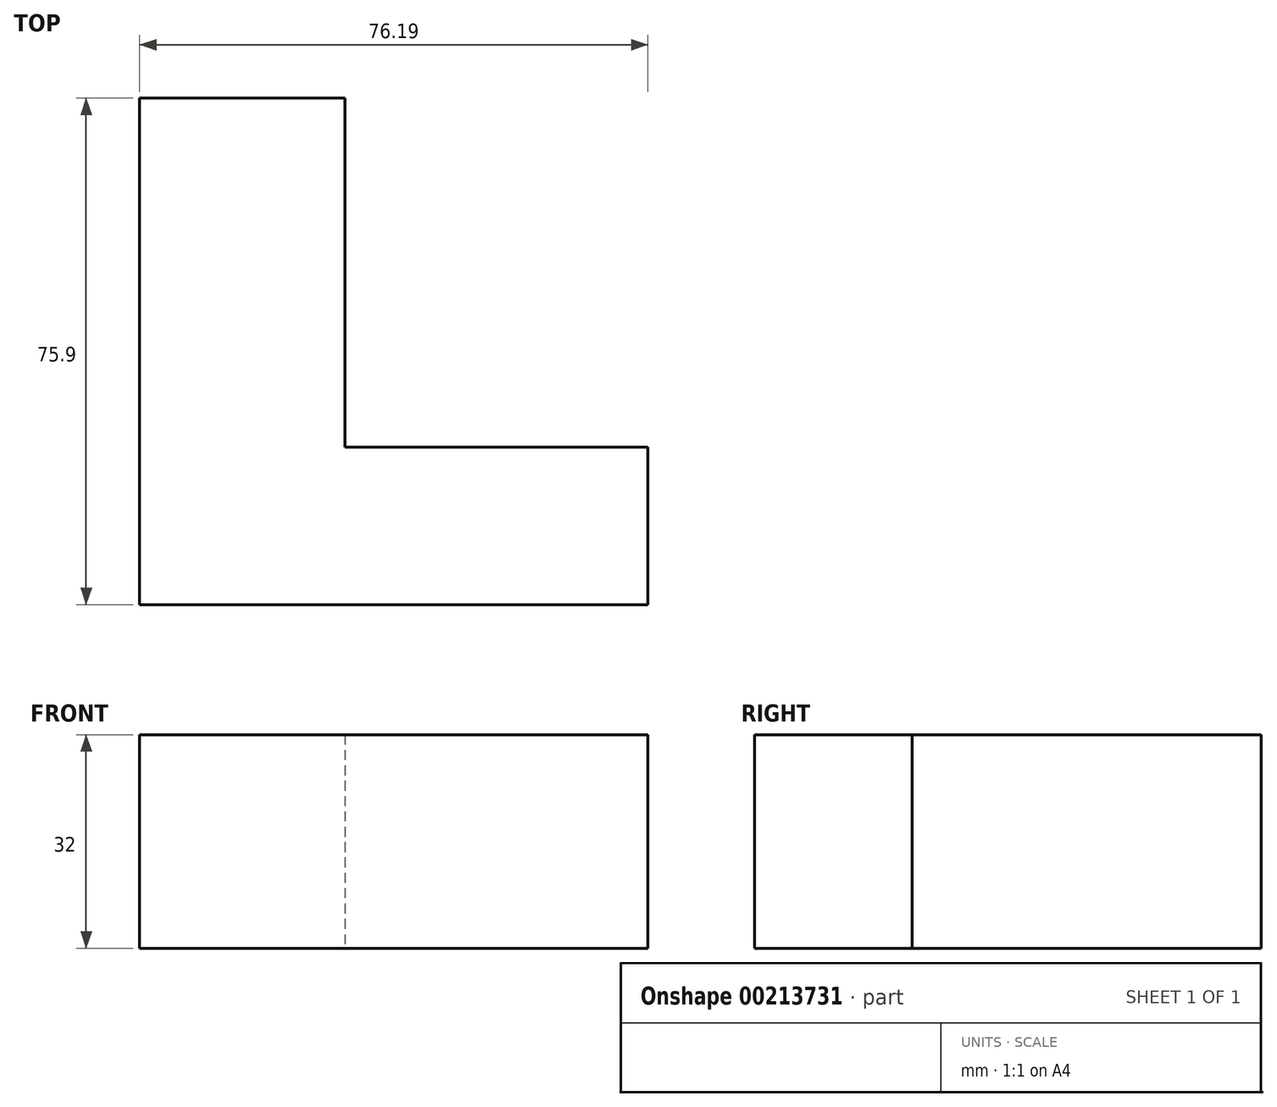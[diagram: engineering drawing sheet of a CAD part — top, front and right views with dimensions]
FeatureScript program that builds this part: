
annotation { "Feature Type Name" : "Feature", "Feature Type Description" : "" }
export const myFeature = defineFeature(function(context is Context, id is Id, definition is map)
    precondition{}
    {
        {
            var Q0;
            Q0=qCreatedBy(makeId("Top.planeOp"),FACE);
            var sketch = newSketch(context, id + "F0", { "sketchPlane" : qUnion([Q0])});
            skLineSegment(sketch, "E0", {"start": v(0, 0) * mm, "end": v(76.2, 0) * mm});
            skLineSegment(sketch, "E1", {"start": v(76.2, 0) * mm, "end": v(76.2, 23.6) * mm});
            skLineSegment(sketch, "E2", {"start": v(76.2, 23.6) * mm, "end": v(30.75, 23.6) * mm});
            skLineSegment(sketch, "E3", {"start": v(30.75, 23.6) * mm, "end": v(30.75, 75.9) * mm});
            skLineSegment(sketch, "E4", {"start": v(30.75, 75.9) * mm, "end": v(0, 75.9) * mm});
            skLineSegment(sketch, "E5", {"start": v(0, 75.9) * mm, "end": v(0, 0) * mm});
            skSolve(sketch);
        }
        {
            var Q0;
            Q0=makeQuery(id+"F0.imprint","IMPRINT",FACE,{"disambiguationData":[TD([[makeQuery(id+"F0.imprint","IMPRINT",EDGE,{"derivedFrom":sQuery(id+"F0.wireOp",EDGE,"E0")}),1.0]])]});
            extrude(context, id + "F1", {"entities" : qUnion([Q0]), "depth" : 32 * mm});
        }
    });
